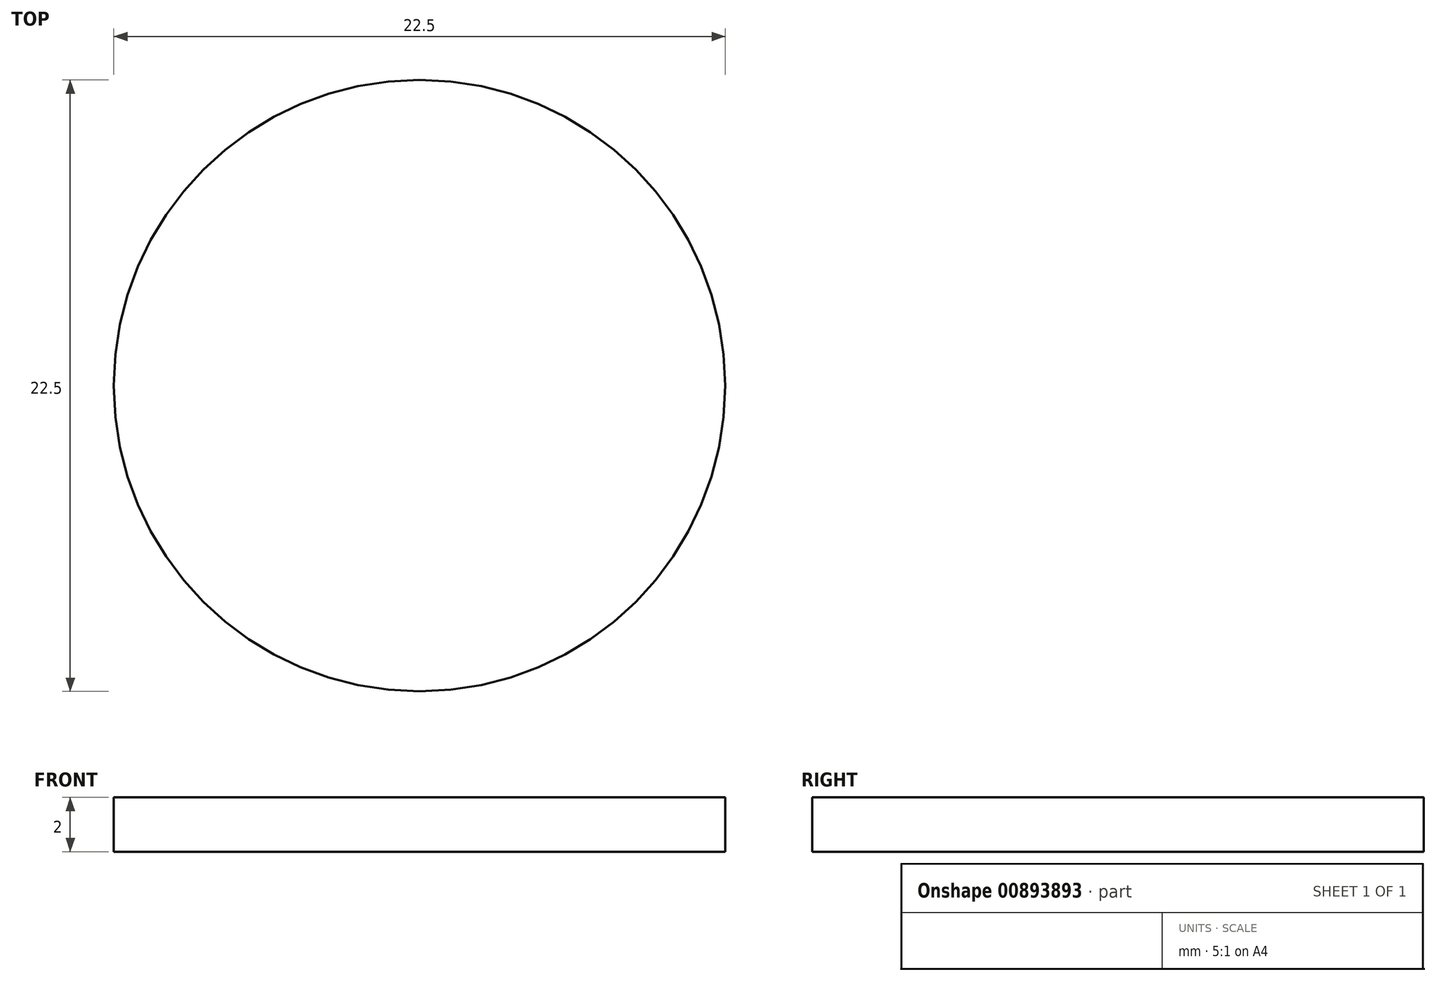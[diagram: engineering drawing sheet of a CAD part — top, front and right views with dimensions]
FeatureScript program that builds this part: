
annotation { "Feature Type Name" : "Feature", "Feature Type Description" : "" }
export const myFeature = defineFeature(function(context is Context, id is Id, definition is map)
    precondition{}
    {
        {
            var Q0;
            Q0=qCreatedBy(makeId("Top.planeOp"),FACE);
            var sketch = newSketch(context, id + "F0", { "sketchPlane" : qUnion([Q0])});
            skCircle(sketch, "E0", {"center": v(0, 0) * mm, "radius": 11.25 * mm});
            skSolve(sketch);
        }
        {
            var Q0;
            Q0=makeQuery(id+"F0.imprint","IMPRINT",FACE,{"disambiguationData":[TD([[makeQuery(id+"F0.imprint","IMPRINT",EDGE,{"derivedFrom":sQuery(id+"F0.wireOp",EDGE,"E0")}),1.0]])]});
            extrude(context, id + "F1", {"entities" : qUnion([Q0]), "depth" : 2 * mm, "offsetDistance" : 25 * mm});
        }
    });
